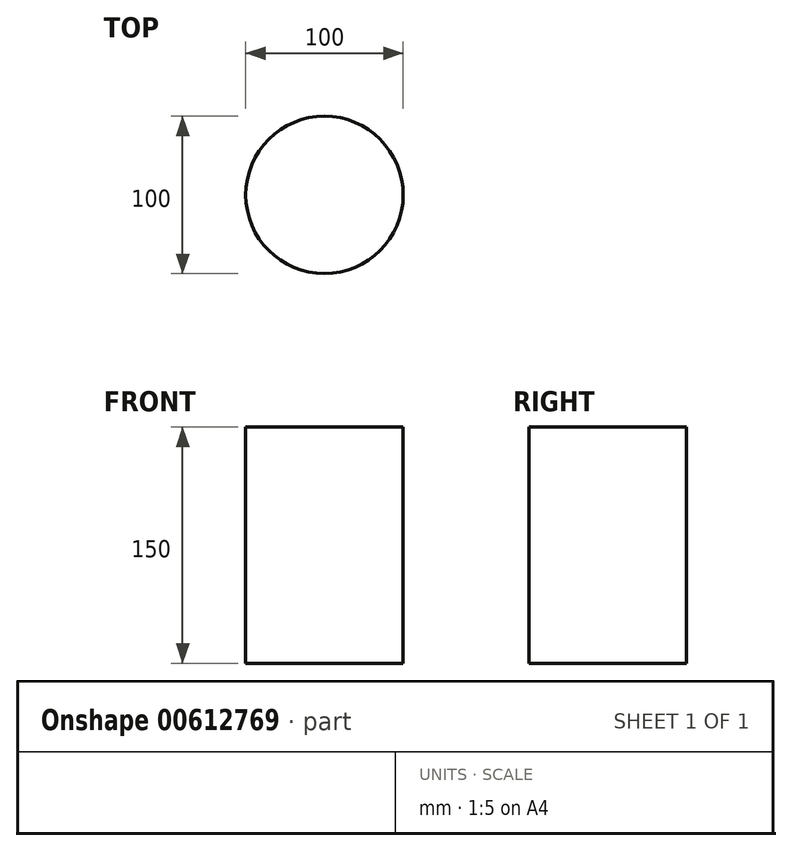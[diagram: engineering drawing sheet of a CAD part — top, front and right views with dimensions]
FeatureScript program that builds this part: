
annotation { "Feature Type Name" : "Feature", "Feature Type Description" : "" }
export const myFeature = defineFeature(function(context is Context, id is Id, definition is map)
    precondition{}
    {
        {
            var Q0;
            Q0=qCreatedBy(makeId("Top.planeOp"),FACE);
            var sketch = newSketch(context, id + "F0", { "sketchPlane" : qUnion([Q0])});
            skCircle(sketch, "E0", {"center": v(0, 0) * mm, "radius": 50 * mm});
            skSolve(sketch);
        }
        {
            var Q0;
            Q0=makeQuery(id+"F0.imprint","IMPRINT",FACE,{"disambiguationData":[TD([[makeQuery(id+"F0.imprint","IMPRINT",EDGE,{"derivedFrom":sQuery(id+"F0.wireOp",EDGE,"E0")}),1.0]])]});
            extrude(context, id + "F1", {"entities" : qUnion([Q0]), "depth" : 150 * mm, "offsetDistance" : 25 * mm});
        }
    });
